# Revit family: NBS_Senator_OffcChrs_Jonny_JNY05
name_source: partatom
category: Furniture
revit_build: Autodesk Revit 2016 (Build: 20151007_0715(x64)
units: mm (PartAtom-declared; Revit-internal decimal feet)

## family parameters
Always vertical = Yes
Cut with Voids When Loaded = No
OmniClass Number = 23.40.20.00
Room Calculation Point = No
Shared = No
Work Plane-Based = No

## types (4) — shared parameters
AssetType = Moveable
Category = Pr_40_50_12_57:Office chairs
CodePerformance = BS EN 16139:2013-L1
DurationUnit = year
FrameColour = Silver, black
FrameFinish = Powder coat
FrameMaterials = Steel
FrameMountingMaterial = NBS_Concept
IfcExportAs = IfcFurnitureType
IfcExportType = CHAIR
IsBuiltIn = No
MainColor = User to populate
ManufacturerName = Senator
ManufacturerURL = www.senator.co.uk
Material = Steel
ModelReference = Jonny stool
NBSCertification = www.nationalbimlibrary.com/cert/sdlqmuy1
NBSDescription = Office chairs
NBSReference = 45-35-20/330
NominalDepth = 610 mm  [stored 2.00131 ft]
NominalLength = 590 mm  [stored 1.9357 ft]
OptionalFeatures = Tubular steel frame available in black powder coat
ProductInformation = www.thesenatorgroup.com/FamilyDocuments/768/SENATOR%20Spec%20Sheet%20-%20Jonny.pdf
SeatArmMaterial = NBS_Concept
SeatFrameMaterial = NBS_Concept
SeatMaterial = NBS_Concept
SeatingSeatBackMaterial = NBS_Concept
SeatingSeatMaterial = NBS_Concept
SeatsAndBacksColourOptions = Black, light grey, graphite, turtle dove, storm,  vintage red, orange crush, citrus, azure blue or aqua
SeatsAndBacksMaterial = Plastic
StandardsDimensions = BS EN 16139: 2013 Level 1
StandardsDurability = BS EN 16139: 2013 Level 1
StandardsSafetyRequirements = BS EN 16139: 2013 Level 1
Status = UNSET
Style = Stool
SustainabilityPerformance = 100% recycleable
Uniclass2015Code = Pr_40_50_12_57
Uniclass2015Title = Office chairs
Uniclass2015Version = Products v1.9
Version = 1
WarrantyDescription = Senator warrants that its manufactured products are free from defects for a period of ten years on Senator seating ranges
WarrantyDurationParts = 10
WarrantyDurationUnit = year
zero-valued in all types: HighestSeatingHeight, LowestSeatingHeight

## per-type parameters (varying)
| type | BIMObjectName | Description | FrameType | HasArms | Name | NominalHeight | SeatHight | SeatingHeight | Size |
| JNY05ACH | NBS_Senator_OfficeChairs_Jonny_JNY05ACH | Plastic seat and back high stool with arms counter height | NBS_Senator_OffcChrs_Jonny_Frame_Medium | Yes | OfficeChairs_Jonny_JNY05ACH_Senator | 1005 mm  [stored 3.29724 ft] | 623 mm  [stored 2.04396 ft] | 590 mm  [stored 1.9357 ft] | 590 x 610 x 1005 mm |
| JNY05CH | NBS_Senator_OfficeChairs_Jonny_JNY05CH | Plastic seat and back high stool counter height | NBS_Senator_OffcChrs_Jonny_Frame_Medium | No | OfficeChairs_Jonny_JNY05CH_Senator | 1005 mm  [stored 3.29724 ft] | 623 mm  [stored 2.04396 ft] | 590 mm  [stored 1.9357 ft] | 590 x 610 x 1005 mm |
| JNY05A | NBS_Senator_OfficeChairs_Jonny_JNY05A | Plastic seat and back high stool with arms | NBS_Senator_OffcChrs_Jonny_Frame_High : NBS_Senator_OffcChrs_Jonny_Frame_Heigh | Yes | OfficeChairs_Jonny_JNY05A_Senator | 1135 mm  [stored 3.72375 ft] | 760 mm | 720 mm  [stored 2.3622 ft] | 590 x 610 x 1135 mm |
| JNY05 | NBS_Senator_OfficeChairs_Jonny_JNY05 | Plastic seat and back high stool | NBS_Senator_OffcChrs_Jonny_Frame_High : NBS_Senator_OffcChrs_Jonny_Frame_Heigh | No | OfficeChairs_Jonny_JNY05_Senator | 1135 mm  [stored 3.72375 ft] | 760 mm | 720 mm  [stored 2.3622 ft] | 590 x 610 x 1135 mm |

note: column(s) folded — value = type name in every type: ModelNumber

note: [stored X ft] marks values corroborated as IEEE doubles in the binary element streams (Revit-internal decimal feet)

## geometry (parser evidence)
native form markers: Sweep x10
no freeform markers — native parametric forms only
